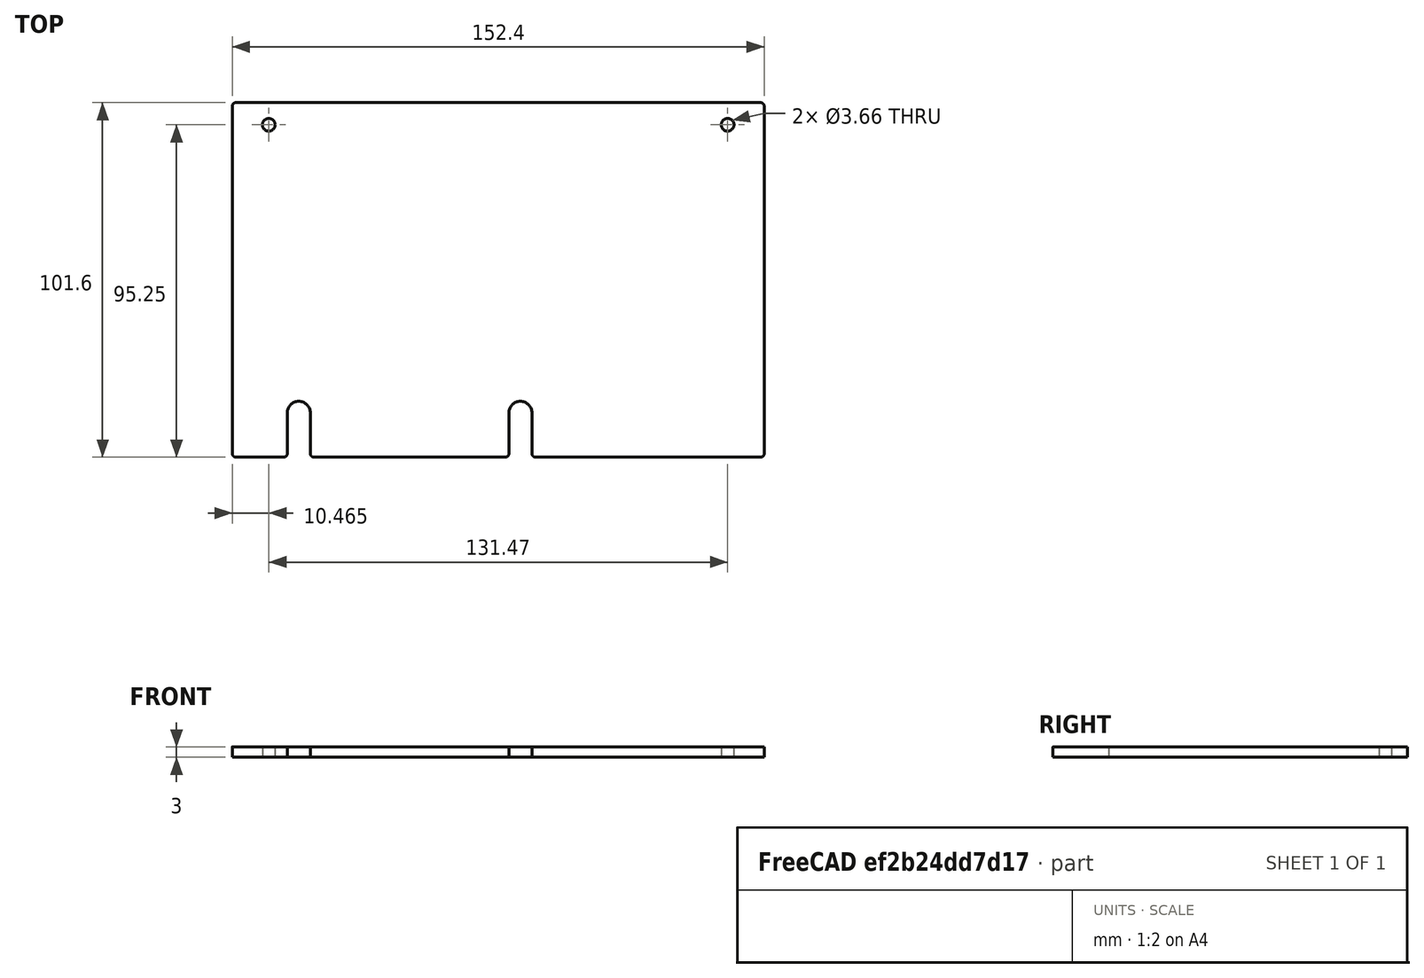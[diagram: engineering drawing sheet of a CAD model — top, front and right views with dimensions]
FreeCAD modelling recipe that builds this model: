
FCSTD DOCUMENT  (FreeCAD 0.21R33675 (Git))
Label: feeding_box_side
License: All rights reserved
LicenseURL: http://en.wikipedia.org/wiki/All_rights_reserved
objects: Sketcher::SketchObject×1, Spreadsheet::Sheet×1, PartDesign::Pad×1, PartDesign::Body×1
note: 4 computed .brp shape members not serialized (recipe doc carries the construction recipe); baked Part::Feature solids carry a one-line shape summary decoded from their .brp

FEATURE [Sketcher::SketchObject] Sketch
  FullyConstrained = true
  MapMode = 5
  Support = -> [XY_Plane]
  expr: Constraints[19] = Spreadsheet.FilletRadius
  expr: Constraints[21] = Spreadsheet.Height
  expr: Constraints[22] = Spreadsheet.Length
  expr: Constraints[29] = Spreadsheet.MountHoleSideMarginSmall
  expr: Constraints[35] = Spreadsheet.MountHoleDistanceFromBottom
  expr: Constraints[38] = Spreadsheet.MountHoleDiameter
  expr: Constraints[42] = Spreadsheet.MountHoleSideMarginLarge
  expr: Constraints[45] = Spreadsheet.BracketHoleFromSide
  expr: Constraints[46] = Spreadsheet.UpperBracketHoleFromTop
  expr: Constraints[48] = Spreadsheet.BracketHoleDiameter
  expr: Constraints[58] = Spreadsheet.BracketHoleFromSide
  expr: Constraints[59] = Spreadsheet.UpperBracketHoleFromTop
  sketch-geometry (40):
    g0: ArcOfCircle CenterX=-75.2 CenterY=49.8 CenterZ=0 NormalX=0 NormalY=0 NormalZ=1 AngleXU=0 Radius=1 StartAngle=1.5708 EndAngle=3.14159
    g1: LineSegment StartX=-75.2 StartY=50.8 StartZ=0 EndX=75.2 EndY=50.8 EndZ=0
    g2: ArcOfCircle CenterX=75.2 CenterY=49.8 CenterZ=0 NormalX=0 NormalY=0 NormalZ=1 AngleXU=0 Radius=1 StartAngle=8e-16 EndAngle=1.5708
    g3: LineSegment StartX=76.2 StartY=49.8 StartZ=0 EndX=76.2 EndY=-49.8 EndZ=0
    g4: ArcOfCircle CenterX=75.2 CenterY=-49.8 CenterZ=0 NormalX=0 NormalY=0 NormalZ=1 AngleXU=0 Radius=1 StartAngle=4.71239 EndAngle=6.28319
    g5: LineSegment StartX=75.2 StartY=-50.8 StartZ=0 EndX=-75.2 EndY=-50.8 EndZ=0
    g6: ArcOfCircle CenterX=-75.2 CenterY=-49.8 CenterZ=0 NormalX=0 NormalY=0 NormalZ=1 AngleXU=0 Radius=1 StartAngle=3.14159 EndAngle=4.71239
    g7: LineSegment StartX=-76.2 StartY=-49.8 StartZ=0 EndX=-76.2 EndY=49.8 EndZ=0
    g8: GeomPoint X=-76.2 Y=50.8 Z=0
    g9: GeomPoint X=76.2 Y=-50.8 Z=0
    g10: LineSegment StartX=-57.15 StartY=-38.1 StartZ=0 EndX=-76.2 EndY=-38.1 EndZ=0
    g11: LineSegment StartX=6.35 StartY=-38.1 StartZ=0 EndX=76.2 EndY=-38.1 EndZ=0
    g12: Circle CenterX=-57.15 CenterY=-38.1 CenterZ=0 NormalX=0 NormalY=0 NormalZ=1 AngleXU=0 Radius=3.302
    g13: Circle CenterX=6.35 CenterY=-38.1 CenterZ=0 NormalX=0 NormalY=0 NormalZ=1 AngleXU=0 Radius=3.302
    g14: LineSegment StartX=0 StartY=-38.1 StartZ=0 EndX=0 EndY=-50.8 EndZ=0
    g15: LineSegment StartX=-57.15 StartY=-38.1 StartZ=0 EndX=0 EndY=-38.1 EndZ=0
    g16: LineSegment StartX=0 StartY=-38.1 StartZ=0 EndX=6.35 EndY=-38.1 EndZ=0
    g17: LineSegment StartX=-65.7352 StartY=50.8 StartZ=0 EndX=-65.7352 EndY=44.45 EndZ=0
    g18: Circle CenterX=-65.7352 CenterY=44.45 CenterZ=0 NormalX=0 NormalY=0 NormalZ=1 AngleXU=0 Radius=1.8288
    g19: LineSegment StartX=-65.7352 StartY=44.45 StartZ=0 EndX=-65.7352 EndY=0 EndZ=0
    g20: LineSegment StartX=-76.2 StartY=1.2e-15 StartZ=0 EndX=-65.7352 EndY=1.2e-15 EndZ=0
    g21: Circle CenterX=-65.7352 CenterY=1.2e-15 CenterZ=0 NormalX=0 NormalY=0 NormalZ=1 AngleXU=0 Radius=1.8288
    g22: LineSegment StartX=65.7352 StartY=50.8 StartZ=0 EndX=65.7352 EndY=44.45 EndZ=0
    g23: LineSegment StartX=65.7352 StartY=44.45 StartZ=0 EndX=65.7352 EndY=7.1e-15 EndZ=0
    g24: LineSegment StartX=65.7352 StartY=5e-15 StartZ=0 EndX=76.2 EndY=5e-15 EndZ=0
    g25: Circle CenterX=65.7352 CenterY=44.45 CenterZ=0 NormalX=0 NormalY=0 NormalZ=1 AngleXU=0 Radius=1.8288
    g26: Circle CenterX=65.7352 CenterY=5e-15 CenterZ=0 NormalX=0 NormalY=0 NormalZ=1 AngleXU=0 Radius=1.8288
    g27: LineSegment StartX=-60.452 StartY=-38.1 StartZ=0 EndX=-60.452 EndY=-49.8 EndZ=0
    g28: ArcOfCircle CenterX=-61.452 CenterY=-49.8 CenterZ=0 NormalX=0 NormalY=0 NormalZ=1 AngleXU=0 Radius=1 StartAngle=4.71239 EndAngle=6.28319
    g29: LineSegment StartX=-53.848 StartY=-38.1 StartZ=0 EndX=-53.848 EndY=-49.8 EndZ=0
    g30: ArcOfCircle CenterX=-52.848 CenterY=-49.8 CenterZ=0 NormalX=0 NormalY=0 NormalZ=1 AngleXU=0 Radius=1 StartAngle=3.14159 EndAngle=4.71239
    g31: LineSegment StartX=3.048 StartY=-38.1 StartZ=0 EndX=3.048 EndY=-49.8 EndZ=0
    g32: LineSegment StartX=9.652 StartY=-38.1 StartZ=0 EndX=9.652 EndY=-49.8 EndZ=0
    g33: ArcOfCircle CenterX=2.048 CenterY=-49.8 CenterZ=0 NormalX=0 NormalY=0 NormalZ=1 AngleXU=0 Radius=1 StartAngle=4.71239 EndAngle=6.28319
    g34: ArcOfCircle CenterX=10.652 CenterY=-49.8 CenterZ=0 NormalX=0 NormalY=0 NormalZ=1 AngleXU=0 Radius=1 StartAngle=3.14159 EndAngle=4.71239
    g35: ArcOfCircle CenterX=-57.15 CenterY=-38.1 CenterZ=0 NormalX=0 NormalY=0 NormalZ=1 AngleXU=0 Radius=3.302 StartAngle=6.28318 EndAngle=9.42478
    g36: ArcOfCircle CenterX=6.35 CenterY=-38.1 CenterZ=0 NormalX=0 NormalY=0 NormalZ=1 AngleXU=0 Radius=3.302 StartAngle=6.28318 EndAngle=9.42478
    g37: LineSegment StartX=-75.2 StartY=-50.8 StartZ=0 EndX=-61.452 EndY=-50.8 EndZ=0
    g38: LineSegment StartX=-52.848 StartY=-50.8 StartZ=0 EndX=2.048 EndY=-50.8 EndZ=0
    g39: LineSegment StartX=10.652 StartY=-50.8 StartZ=0 EndX=75.2 EndY=-50.8 EndZ=0
  constraints (101):
    c: Tangent(g0,g1) = 1.5708
    c: Tangent(g1,g2) = 1.5708
    c: Tangent(g2,g3) = 1.5708
    c: Tangent(g3,g4) = 1.5708
    c: Tangent(g4,g5) = 1.5708
    c: Tangent(g5,g6) = 1.5708
    c: Tangent(g6,g7) = 1.5708
    c: Tangent(g7,g0) = 1.5708
    c: Horizontal(g1)
    c: Horizontal(g5)
    c: Vertical(g3)
    c: Vertical(g7)
    c: Equal(g0,g2)
    c: Equal(g2,g4)
    c: Equal(g4,g6)
    c: PointOnObject(g8,g1)
    c: PointOnObject(g8,g7)
    c: PointOnObject(g9,g3)
    c: PointOnObject(g9,g5)
    c: Radius(g2) = 1
    c: Symmetric(g8,g9,g-1)
    c: DistanceY(g4,g1) = 101.6
    c: DistanceX(g0,g2) = 152.4
    c: PointOnObject(g14,g5)
    c: PointOnObject(g14,g-2)
    c: PointOnObject(g10,g7)
    c: Horizontal(g10)
    c: PointOnObject(g11,g3)
    c: Horizontal(g11)
    c: DistanceX(g10,g10) = 19.05
    c: Vertical(g14)
    c: Coincident(g15,g12)
    c: Horizontal(g15)
    c: Coincident(g16,g13)
    c: Horizontal(g16)
    c: DistanceY(g14,g14) = 12.7
    c: Coincident(g10,g12)
    c: Coincident(g13,g11)
    c: Diameter(g13) = 6.604
    c: Coincident(g16,g14)
    c: Coincident(g15,g14)
    c: Equal(g12,g13)
    c: DistanceX(g11,g11) = 69.85
    c: PointOnObject(g17,g1)
    c: Vertical(g17)
    c: DistanceX(g8,g17) = 10.4648
    c: DistanceY(g17,g17) = 6.35
    c: Coincident(g18,g17)
    c: Diameter(g18) = 3.6576
    c: Coincident(g19,g18)
    c: Vertical(g19)
    c: Horizontal(g20)
    c: Symmetric(g6,g0,g20)
    c: Coincident(g19,g20)
    c: Coincident(g21,g19)
    c: Equal(g21,g18)
    c: PointOnObject(g22,g1)
    c: Vertical(g22)
    c: DistanceX(g22,g2) = 10.4648
    c: DistanceY(g22,g22) = 6.35
    c: Coincident(g23,g22)
    c: Vertical(g23)
    c: Coincident(g24,g23)
    c: Horizontal(g24)
    c: Symmetric(g2,g3,g24)
    c: Coincident(g25,g22)
    c: Coincident(g26,g23)
    c: Equal(g18,g26)
    c: Equal(g18,g25)
    c: Vertical(g27)
    c: Tangent(g27,g12) = -1.5708
    c: Tangent(g28,g27) = 1.5708
    c: Tangent(g28,g5) = 1.5708
    c: Equal(g28,g4)
    c: Vertical(g29)
    c: Tangent(g29,g12) = 1.5708
    c: Tangent(g30,g29) = -1.5708
    c: Tangent(g30,g5) = 1.5708
    c: Equal(g30,g4)
    c: Vertical(g31)
    c: Vertical(g32)
    c: Tangent(g31,g13) = -1.5708
    c: Tangent(g32,g13) = 1.5708
    c: Tangent(g33,g31) = 1.5708
    c: Tangent(g33,g5) = 1.5708
    c: Equal(g33,g4)
    c: Tangent(g34,g32) = -1.5708
    c: Tangent(g34,g5) = 1.5708
    c: Equal(g34,g4)
    c: Coincident(g35,g27)
    c: Coincident(g35,g29)
    c: Equal(g35,g12)
    c: Coincident(g36,g31)
    c: Coincident(g32,g36)
    c: Equal(g36,g13)
    c: Coincident(g6,g37)
    c: Coincident(g37,g28)
    c: Coincident(g30,g38)
    c: Coincident(g38,g33)
    c: Coincident(g39,g34)
    c: Coincident(g4,g39)
FEATURE [Spreadsheet::Sheet] Spreadsheet
  cells = A2='Parameters; A3='Height; B3(Height)==4 in; A4='Length; B4(Length)==6 in; A5='Thickness; B5(Thickness)==3 mm; A6='FilletRadius; B6(FilletRadius)==1 mm; A7='MountHoleDiameter; B7(MountHoleDiameter)==0.26 in; A8='MountHoleDistanceFromBottom; B8(MountHoleDistanceFromBottom)==0.5 in; A9='MountHoleSideMarginSmall; B9(MountHoleSideMarginSmall)==0.75 in; A10='MountHoleSideMarginLarge; B10(MountHoleSideMarginLarge)==2.75 in; A11='BeamHeight; B11(BeamHeight)==1 in; A12='FloorHeight; B12(FloorHeight)==BeamHeight + 0.125 in; A14='BracketWidth; B14(BracketWidth)==0.5 in; A15='BracketHoleDiameter; B15(BracketHoleDiameter)==0.144 in; A16='BracketHoleOffset; B16(BracketHoleOffset)==0.412 in; A17='UpperBracketHoleFromTop; B17(UpperBracketHoleFromTop)==0.5 * BracketWidth; A18='BracketHoleFromSide; B18(BracketHoleFromSide)==BracketHoleOffset
FEATURE [PartDesign::Pad] Pad
  Direction = (0,0,1)
  Length = 3
  Length2 = 10
  Profile = -> Sketch
  ReferenceAxis = -> Sketch [N_Axis]
  Type = 0
  expr: Length = Spreadsheet.Thickness
FEATURE [PartDesign::Body] Body
  Group = -> [Sketch,Pad]
  Origin = -> Origin
  Tip = -> Pad
